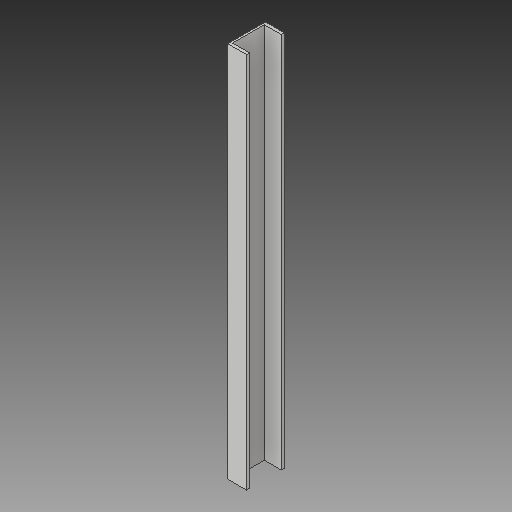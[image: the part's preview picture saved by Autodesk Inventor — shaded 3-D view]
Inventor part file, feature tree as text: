
AUTODESK INVENTOR PART (.ipt)
format: ipt  version: 2019 (Build 230136000, 136)  size: 87,040 bytes
history: native  units: in
note: dims shown in document units (in); Inventor stores cm internally (conversion verified against a paired STEP export)
features: other x3, sketch x1
ambient origin geometry x8: Origin, YZ Plane, XZ Plane, XY Plane, X Axis, Y Axis, Z Axis, Center Point
bodies: Solid1 (feature_tree)
feature tree (4):
  other  "Channel1_MIR1.ipt"
  other  "Solid1::Channel1_MIR1.ipt"
  other  "TaggingFeature1"
  sketch  "Sketch1"  dims[d0=0.3937in]
